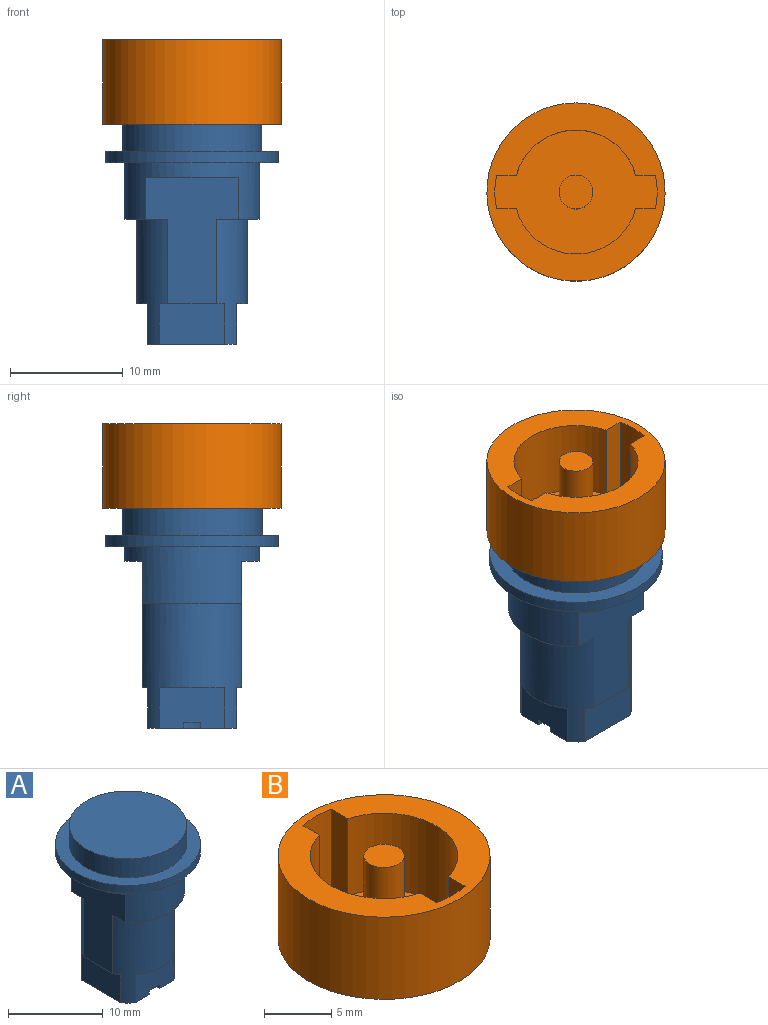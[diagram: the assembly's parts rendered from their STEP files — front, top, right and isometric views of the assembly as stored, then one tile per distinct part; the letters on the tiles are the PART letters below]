
ASSEMBLY  parts=2 mates=1
PART A: 29 faces, bbox 15.3x15.3x19.5 mm
  f0: plane 15.3x15.3mm, normal (0,0,1), area 63.1mm2, adj f3,f28
  f1: cylinder r=3.1mm len=6.2mm, axis (0,0,1), area 9mm2, adj f9,f11,f12,f13
  f2: cylinder r=6mm len=12mm, axis (0,0,-1), area 122.1mm2, adj f4,f5,f6,f7,f15,f16,f18
  f3: cylinder r=7.65mm len=15.3mm, axis (0,0,1), area 48.1mm2, adj f0,f6
  f4: plane 11.2x8.16mm, normal (1,0,0), area 62.5mm2, adj f2,f7,f8,f16,f17,f18,f22
  f5: plane 11.2x8.16mm, normal (-1,0,0), area 62.5mm2, adj f2,f7,f8,f15,f17,f18,f20
  f6: plane 15.3x15.3mm, normal (0,0,-1), area 70.8mm2, adj f2,f3
  f7: plane 8.8x3.84mm, normal (0,0,-1), area 11.3mm2, adj f2,f4,f5,f8
  f8: cylinder r=4.9mm len=11.1mm, axis (0,0,-1), area 92.7mm2, adj f4,f5,f7,f9,f10,f14,f19,f20
  f9: plane 7.9x7.9mm, normal (0,0,-1), area 28.9mm2, adj f1,f8,f10,f12,f13,f17,f19,f21
  f10: plane 5.8x3.6mm, normal (0,-1,0), area 20.1mm2, adj f8,f9,f11,f12,f13,f14
  f11: plane 7.05x6.2mm, normal (0,0,-1), area 11.9mm2, adj f1,f10,f12,f13,f26
  f12: plane 0.94x0.5mm, normal (-1,0,0), area 0.5mm2, adj f1,f9,f10,f11
  f13: plane 0.94x0.5mm, normal (1,0,0), area 0.5mm2, adj f1,f9,f10,f11
  f14: plane 5.8x0.95mm, normal (0,0,-1), area 3.8mm2, adj f8,f10
  f15: plane 8.16x1.6mm, normal (0,0,-1), area 9mm2, adj f2,f5
  f16: plane 8.16x1.6mm, normal (0,0,-1), area 9mm2, adj f2,f4
  f17: cylinder r=4.9mm len=11.1mm, axis (0,0,1), area 92.7mm2, adj f4,f5,f9,f18,f19,f20,f21,f22
  f18: plane 8.8x3.84mm, normal (0,0,-1), area 11.3mm2, adj f2,f4,f5,f17
  f19: plane 5.8x3.6mm, normal (-1,0,0), area 20.9mm2, adj f8,f9,f17,f20
  f20: plane 5.8x0.45mm, normal (0,0,-1), area 2.3mm2, adj f5,f8,f17,f19
  f21: plane 5.8x3.6mm, normal (1,0,0), area 20.9mm2, adj f8,f9,f17,f22
  f22: plane 5.8x0.45mm, normal (0,0,-1), area 2.3mm2, adj f4,f8,f17,f21
  f23: plane 5.8x3.6mm, normal (0,1,0), area 20.9mm2, adj f9,f17,f24
  f24: plane 5.8x0.95mm, normal (0,0,-1), area 3.8mm2, adj f17,f23
  f25: plane 12.4x12.4mm, normal (0,0,1), area 120.8mm2, adj f28
  f26: cylinder r=2.5mm len=13mm, axis (0,0,1), area 204.2mm2, adj f11,f27
  f27: cone r=2.5mm half-angle=59deg, axis (0,0,-1), area 22.9mm2, adj f26
  f28: cylinder r=6.2mm len=12.4mm, axis (0,0,1), area 93.5mm2, adj f0,f25
PART B: 14 faces, bbox 15.8x15.8x7.5 mm
  f0: cylinder r=1.5mm len=7mm, axis (0,0,-1), area 66mm2, adj f1,f2
  f1: plane 14.4x11mm, normal (0,0,1), area 98.3mm2, adj f0,f3,f4,f8,f9,f10,f11,f12
  f2: plane 3x3mm, normal (0,0,1), area 7.1mm2, adj f0
  f3: plane 7x1.75mm, normal (-1,0,0), area 12.3mm2, adj f1,f5,f11,f13
  f4: plane 7x1.75mm, normal (-1,0,0), area 12.3mm2, adj f1,f5,f9,f13
  f5: plane 15.8x15.8mm, normal (0,0,1), area 90.7mm2, adj f3,f4,f6,f8,f9,f10,f11,f12
  f6: cylinder r=7.9mm len=15.8mm, axis (0,0,1), area 372.3mm2, adj f5,f7
  f7: plane 15.8x15.8mm, normal (0,0,-1), area 196.1mm2, adj f6
  f8: cylinder r=5.5mm len=10.58mm, axis (0,0,-1), area 99.7mm2, adj f1,f5,f10,f12
  f9: cylinder r=7.2mm len=7mm, axis (0,0,-1), area 21.2mm2, adj f1,f4,f5,f10
  f10: plane 7x1.75mm, normal (1,0,0), area 12.3mm2, adj f1,f5,f8,f9
  f11: cylinder r=7.2mm len=7mm, axis (0,0,-1), area 21.2mm2, adj f1,f3,f5,f12
  f12: plane 7x1.75mm, normal (1,0,0), area 12.3mm2, adj f1,f5,f8,f11
  f13: cylinder r=5.5mm len=10.58mm, axis (0,0,-1), area 99.7mm2, adj f1,f3,f4,f5
PLACE A rot(axis=(0,0,-1),90deg) t=(0,0.05,-66.66)mm
PLACE B rot(axis=(0,0,-1),90deg) t=(0,0.05,-66.66)mm
MATE fastened B.f6 <-> A.f2  axis (0,0,-1) through (0,0.05,19.57)mm
